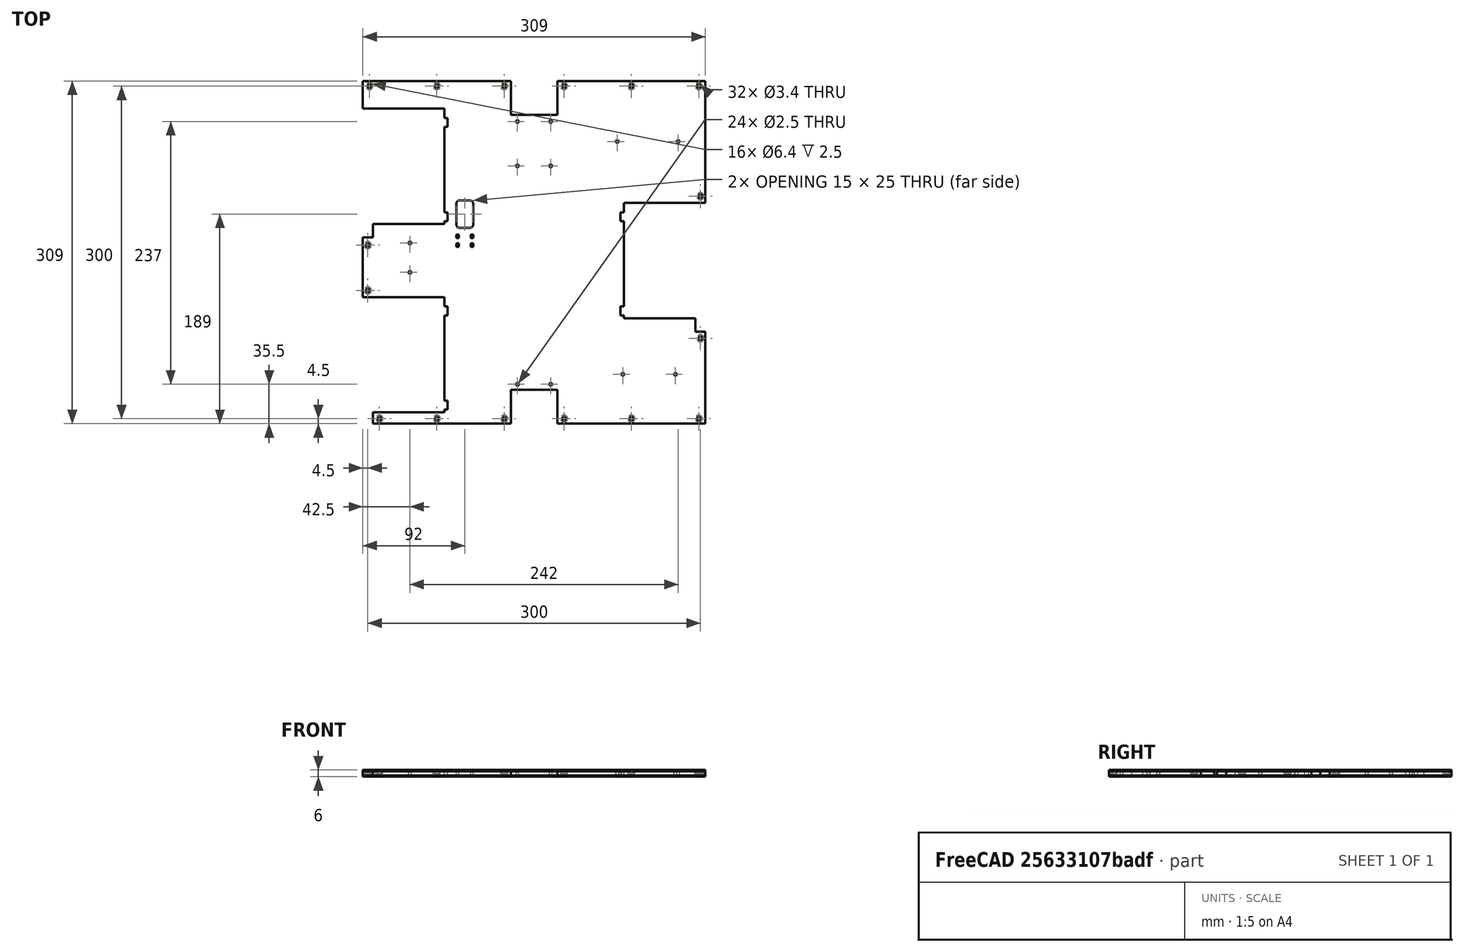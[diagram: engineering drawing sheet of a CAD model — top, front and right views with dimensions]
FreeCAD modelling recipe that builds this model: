
FCSTD DOCUMENT  (FreeCAD 0.19R24291 (Git))
Label: bottom-plate-180-laser-cut
License: All rights reserved
LicenseURL: http://en.wikipedia.org/wiki/All_rights_reserved
objects: Part::Feature×21, Part::Cylinder×12, Part::MultiFuse×9, Part::Cut×6, Part::Box×3, Part::Extrusion×1
note: 52 computed .brp shape members not serialized (recipe doc carries the construction recipe); baked Part::Feature solids carry a one-line shape summary decoded from their .brp

FEATURE [Part::Cylinder] Cylinder016
  Angle = 360
  AttacherType = Attacher::AttachEngine3D
  Height = 6
  Placement = pos=(80,-110,0) rot=(0,0,1;0rad)
  Radius = 1.25
FEATURE [Part::Cylinder] Cylinder011
  Angle = 360
  AttacherType = Attacher::AttachEngine3D
  Height = 10
  Placement = pos=(-15,78,0) rot=(0,0,1;0rad)
  Radius = 1.25
FEATURE [Part::Cylinder] Cylinder009
  Angle = 360
  AttacherType = Attacher::AttachEngine3D
  Height = 10
  Placement = pos=(15,118,0) rot=(0,0,1;0rad)
  Radius = 1.25
FEATURE [Part::Cylinder] Cylinder012
  Angle = 360
  AttacherType = Attacher::AttachEngine3D
  Height = 6
  Placement = pos=(-112,8.5,0) rot=(0,0,1;0rad)
  Radius = 1.25
FEATURE [Part::Feature] Fusion005030019  label="bolt-slot_D004"
  Placement = pos=(-139.5,-150,0) rot=(0,0,1;0rad)
  shape: bbox 6.4 x 6.4 x 6 mm, 7 faces (baked)
FEATURE [Part::Feature] Fusion005030017  label="bolt-slot_D002"
  Placement = pos=(-27,-150,0) rot=(0,0,1;0rad)
  shape: bbox 6.4 x 6.4 x 6 mm, 7 faces (baked)
FEATURE [Part::Cylinder] Cylinder013
  Angle = 360
  AttacherType = Attacher::AttachEngine3D
  Height = 6
  Placement = pos=(-112,-18,0) rot=(0,0,1;0rad)
  Radius = 1.25
FEATURE [Part::Feature] Fusion005030018  label="bolt-slot_D003"
  Placement = pos=(148.5,-150,0) rot=(0,0,1;0rad)
  shape: bbox 6.4 x 6.4 x 6 mm, 7 faces (baked)
FEATURE [Part::Feature] Fusion005030028  label="bolt-slot_R002"
  Placement = pos=(150,-77.5,0) rot=(0,0,1;0rad)
  shape: bbox 6.4 x 6.4 x 6 mm, 7 faces (baked)
FEATURE [Part::Box] Box003  label="Cube003"
  AttacherType = Attacher::AttachEngine3D
  Height = 10
  Length = 42
  Placement = pos=(-21,124,0) rot=(0,0,1;0rad)
  Width = 31
FEATURE [Part::Feature] Fusion005030016  label="bolt-slot_D001"
  Placement = pos=(27,-150,0) rot=(0,0,1;0rad)
  shape: bbox 6.4 x 6.4 x 6 mm, 7 faces (baked)
FEATURE [Part::Feature] Fusion005030021  label="bolt-slot_D006"
  Placement = pos=(-87.75,-150,0) rot=(0,0,1;0rad)
  shape: bbox 6.4 x 6.4 x 6 mm, 7 faces (baked)
FEATURE [Part::Feature] Fusion005030001  label="bed-cable"
  Placement = pos=(35,-24,0) rot=(0,0,1;0rad)
  shape: bbox 15 x 42 x 10 mm, 34 faces, 5 solids (baked)
FEATURE [Part::Feature] Fusion005030025  label="bolt-slot_L003"
  Placement = pos=(-150,-34.36,0) rot=(0,0,1;0rad)
  shape: bbox 6.4 x 6.4 x 6 mm, 7 faces (baked)
FEATURE [Part::Feature] Fusion005030023  label="bolt-slot_L001"
  Placement = pos=(-150,6.5,0) rot=(0,0,1;0rad)
  shape: bbox 6.4 x 6.4 x 6 mm, 7 faces (baked)
FEATURE [Part::Feature] Fusion005030027  label="bolt-slot_R001"
  Placement = pos=(150,50.64,0) rot=(0,0,1;0rad)
  shape: bbox 6.4 x 6.4 x 6 mm, 7 faces (baked)
FEATURE [Part::Cylinder] Cylinder014
  Angle = 360
  AttacherType = Attacher::AttachEngine3D
  Height = 6
  Placement = pos=(75,100,0) rot=(0,0,1;0rad)
  Radius = 1.25
FEATURE [Part::Box] Box002  label="Cube002"
  AttacherType = Attacher::AttachEngine3D
  Height = 10
  Length = 42
  Placement = pos=(-21,-155,0) rot=(0,0,1;0rad)
  Width = 31
FEATURE [Part::Feature] Fusion005030010  label="bolt-slot_U002"
  Placement = pos=(27,150,0) rot=(0,0,1;0rad)
  shape: bbox 6.4 x 6.4 x 6 mm, 7 faces (baked)
FEATURE [Part::Feature] Part__Mirroring001  label="motor-cut-slot (Mirror #1)001"
  Placement = pos=(0,85,0) rot=(0,0,1;0rad)
  shape: bbox 77 x 116.1 x 10 mm, 16 faces (baked)
FEATURE [Part::Feature] Cut001003002002  label="motor-cut-slot001"
  Placement = pos=(-155,15,0) rot=(0,0,1;0rad)
  shape: bbox 77 x 116.1 x 10 mm, 16 faces (baked)
FEATURE [Part::Cylinder] Cylinder
  Angle = 360
  AttacherType = Attacher::AttachEngine3D
  Height = 10
  Placement = pos=(-15,-119,0) rot=(0,0,1;0rad)
  Radius = 1.25
FEATURE [Part::MultiFuse] Fusion001
  Shapes = -> [Box003,Box002]
FEATURE [Part::Cylinder] Cylinder001
  Angle = 360
  AttacherType = Attacher::AttachEngine3D
  Height = 10
  Placement = pos=(15,-119,0) rot=(0,0,1;0rad)
  Radius = 1.25
FEATURE [Part::Cylinder] Cylinder010
  Angle = 360
  AttacherType = Attacher::AttachEngine3D
  Height = 10
  Placement = pos=(15,78,0) rot=(0,0,1;0rad)
  Radius = 1.25
FEATURE [Part::Feature] Fusion005030009  label="bolt-slot_U001"
  Placement = pos=(-27,150,0) rot=(0,0,1;0rad)
  shape: bbox 6.4 x 6.4 x 6 mm, 7 faces (baked)
FEATURE [Part::Feature] Fusion005030012  label="bolt-slot_U004"
  Placement = pos=(148.5,150,0) rot=(0,0,1;0rad)
  shape: bbox 6.4 x 6.4 x 6 mm, 7 faces (baked)
FEATURE [Part::Cylinder] Cylinder017
  Angle = 360
  AttacherType = Attacher::AttachEngine3D
  Height = 6
  Placement = pos=(127.5,-110,0) rot=(0,0,1;0rad)
  Radius = 1.25
FEATURE [Part::Feature] Fusion005030014  label="bolt-slot_U006"
  Placement = pos=(87.75,150,0) rot=(0,0,1;0rad)
  shape: bbox 6.4 x 6.4 x 6 mm, 7 faces (baked)
FEATURE [Part::Feature] Fusion005030020  label="bolt-slot_D005"
  Placement = pos=(87.75,-150,0) rot=(0,0,1;0rad)
  shape: bbox 6.4 x 6.4 x 6 mm, 7 faces (baked)
FEATURE [Part::MultiFuse] Fusion005030022
  Shapes = -> [Fusion005030021,Fusion005030016,Fusion005030017,Fusion005030018,Fusion005030019,Fusion005030020]
FEATURE [Part::Feature] Fusion005030013  label="bolt-slot_U005"
  Placement = pos=(-87.75,150,0) rot=(0,0,1;0rad)
  shape: bbox 6.4 x 6.4 x 6 mm, 7 faces (baked)
FEATURE [Part::Box] Box  label="Cube"
  AttacherType = Attacher::AttachEngine3D
  Height = 5
  Length = 309
  Placement = pos=(-154.5,-154.5,0) rot=(0,0,1;0rad)
  Width = 309
FEATURE [Part::Cylinder] Cylinder015
  Angle = 360
  AttacherType = Attacher::AttachEngine3D
  Height = 6
  Placement = pos=(130,100,0) rot=(0,0,1;0rad)
  Radius = 1.25
FEATURE [Part::MultiFuse] Fusion005030029
  Shapes = -> [Fusion005030028,Fusion005030027]
FEATURE [Part::Feature] Cut001003002001  label="motor-cut-slot"
  Placement = pos=(-155,-155,0) rot=(0,0,1;0rad)
  shape: bbox 77 x 116.1 x 10 mm, 16 faces (baked)
FEATURE [Part::MultiFuse] Fusion
  Shapes = -> [Part__Mirroring001,Cut001003002002,Cut001003002001]
FEATURE [Part::Cut] Cut
  Base = -> Box
  Tool = -> Fusion
FEATURE [Part::Cut] Cut001003002003
  Base = -> Cut
  Tool = -> Fusion001
FEATURE [Part::Feature] Fusion005030011  label="bolt-slot_U003"
  Placement = pos=(-148.5,150,0) rot=(0,0,1;0rad)
  shape: bbox 6.4 x 6.4 x 6 mm, 7 faces (baked)
FEATURE [Part::MultiFuse] Fusion005030015
  Shapes = -> [Fusion005030009,Fusion005030010,Fusion005030011,Fusion005030012,Fusion005030013,Fusion005030014]
FEATURE [Part::Cylinder] Cylinder008
  Angle = 360
  AttacherType = Attacher::AttachEngine3D
  Height = 10
  Placement = pos=(-15,118,0) rot=(0,0,1;0rad)
  Radius = 1.25
FEATURE [Part::MultiFuse] Fusion005030031
  Shapes = -> [Cylinder015,Cylinder017,Cylinder014,Cylinder013,Cylinder012,Cylinder016]
FEATURE [Part::MultiFuse] Fusion005030032
  Shapes = -> [Fusion005030025,Fusion005030023]
FEATURE [Part::MultiFuse] Fusion005030033
  Shapes = -> [Fusion005030032,Fusion005030022,Fusion005030029,Fusion005030015]
FEATURE [Part::Cut] Cut001003002004
  Base = -> Cut001003002003
  Tool = -> Fusion005030001
FEATURE [Part::Cut] Cut001003002005
  Base = -> Cut001003002004
  Tool = -> Fusion005030033
FEATURE [Part::Cut] Cut001003002006
  Base = -> Cut001003002005
  Tool = -> Fusion005030031
FEATURE [Part::MultiFuse] Fusion005030034
  Shapes = -> [Cylinder008,Cylinder011,Cylinder009,Cylinder,Cylinder001,Cylinder010]
FEATURE [Part::Cut] Cut001003002007
  Base = -> Cut001003002006
  Tool = -> Fusion005030034
FEATURE [Part::Feature] Cut001003002007_cs
  shape: bbox 309 x 309 x 3e-07 mm, 0 faces, 0 solids (baked)
FEATURE [Part::Extrusion] Extrude
  Base = -> Cut001003002007_cs
  Dir = (0,0,1)
  DirMode = 2
  FaceMakerClass = Part::FaceMakerBullseye
  LengthFwd = 5
  LengthRev = 0
  Solid = true
  Symmetric = false
